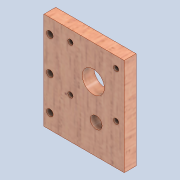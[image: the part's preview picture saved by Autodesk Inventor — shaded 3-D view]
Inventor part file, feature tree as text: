
AUTODESK INVENTOR PART (.ipt)
format: ipt  version: 2020 (Build 240168000, 168)  size: 236,544 bytes
history: native  units: mm
features: sketch x4, extrude x3, hole x1
ambient origin geometry x8: Origin, YZ Plane, XZ Plane, XY Plane, X Axis, Y Axis, Z Axis, Center Point
bodies: Solid1 (feature_tree)
feature tree (8):
  extrude  "Extrusion1"  Depth=66.0mm
  extrude  "Extrusion2"  TaperAngle=0.0deg  [1 undecoded]
  extrude  "Extrusion4"  Depth=21.0mm
  hole  "Hole1"  [1 undecoded]
  sketch  "Sketch1"  dims[d0=54.5mm d1=66.0mm]
  sketch  "Sketch2"  dims[d2=8.0mm d3=0.0mm d6=0.0mm d7=0.0mm]
  sketch  "Sketch4"  dims[d17=15.0mm d19=21.0mm]
  sketch  "Sketch5"  dims[d20=23.0mm d22=31.0mm d23=3.5mm d24=8.0mm d25=20.0mm d26=19.030905mm d27=0.0mm d28=0.0mm d29=4.0mm d30=23.0mm d31=23.0mm d32=4.5mm d33=6.0mm d34=4.0mm d35=2.0mm d36=90.0deg d37=8.0mm d38=20.594885mm]
note: 2 required parameter values undecoded (feature->parameter linkage not recoverable at this tier; creation-order binding heuristic only, values carry confidence <= 0.55)
